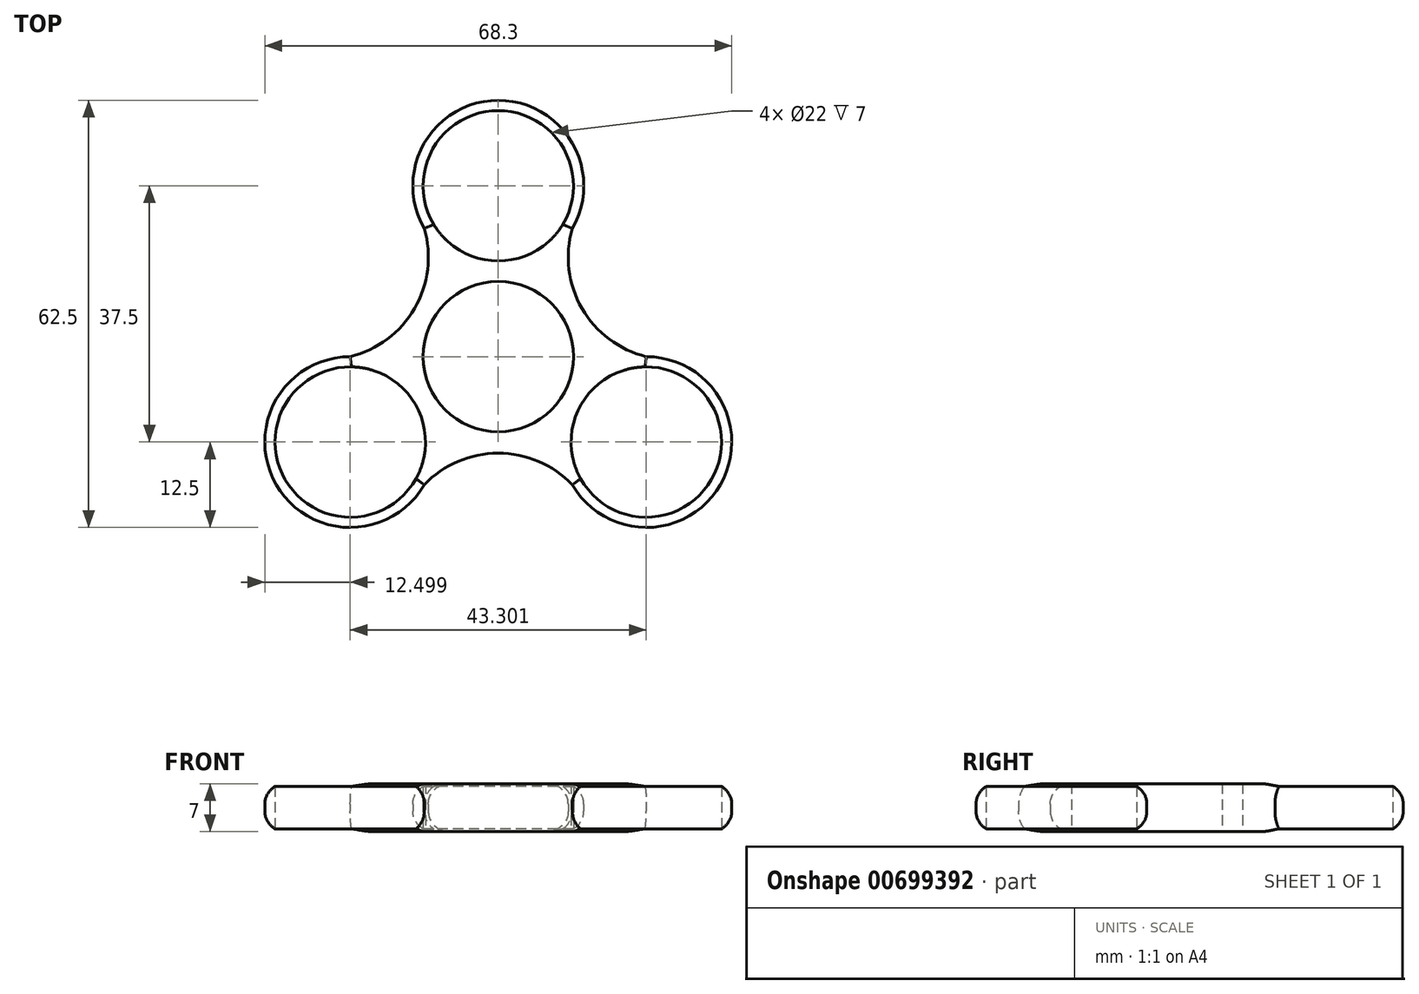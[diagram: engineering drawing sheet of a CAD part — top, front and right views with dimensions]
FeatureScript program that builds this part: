
annotation { "Feature Type Name" : "Feature", "Feature Type Description" : "" }
export const myFeature = defineFeature(function(context is Context, id is Id, definition is map)
    precondition{}
    {
        {
            var Q0;
            Q0=qCreatedBy(makeId("Top.planeOp"),FACE);
            var sketch = newSketch(context, id + "F0", { "sketchPlane" : qUnion([Q0])});
            skCircle(sketch, "E0", {"center": v(0, 0) * mm, "radius": 11 * mm});
            skCircle(sketch, "E1", {"center": v(0, 25) * mm, "radius": 11 * mm});
            skCircle(sketch, "E2", {"center": v(21.65, -12.5) * mm, "radius": 11 * mm});
            skCircle(sketch, "E3", {"center": v(-21.65, -12.5) * mm, "radius": 11 * mm});
            skArc(sketch, "E4", {"start": v(-21.65, 0) * mm, "mid": v(-32.48, -18.75) * mm, "end": v(-10.83, -18.75) * mm});
            skArc(sketch, "E5", {"start": v(10.83, -18.75) * mm, "mid": v(32.48, -18.75) * mm, "end": v(21.65, 0) * mm});
            skArc(sketch, "E6", {"start": v(10.83, 18.75) * mm, "mid": v(0, 37.5) * mm, "end": v(-10.83, 18.75) * mm});
            skArc(sketch, "E7", {"start": v(-21.65, 0) * mm, "mid": v(-12.24, 7.07) * mm, "end": v(-10.83, 18.75) * mm});
            skArc(sketch, "E8", {"start": v(10.83, 18.75) * mm, "mid": v(12.24, 7.07) * mm, "end": v(21.65, 0) * mm});
            skArc(sketch, "E9", {"start": v(10.83, -18.75) * mm, "mid": v(0, -14.13) * mm, "end": v(-10.83, -18.75) * mm});
            skSolve(sketch);
        }
        {
            var Q0;
            Q0=makeQuery(id+"F0.imprint","IMPRINT",FACE,{"disambiguationData":[TD([[makeQuery(id+"F0.imprint","IMPRINT",EDGE,{"derivedFrom":sQuery(id+"F0.wireOp",EDGE,"E0")}),-1.0]])]});
            extrude(context, id + "F1", {"entities" : qUnion([Q0]), "depth" : 7 * mm, "offsetDistance" : 25 * mm});
        }
        {
            var Q0;
            Q0=makeQuery(id+"F1.opExtrude","CAP_EDGE",EDGE,{"disambiguationData":[OSD([sQuery(id+"F0.wireOp",EDGE,"E4")])],"isStart":false});
            var Q1;
            Q1=makeQuery(id+"F1.opExtrude","CAP_EDGE",EDGE,{"disambiguationData":[OSD([sQuery(id+"F0.wireOp",EDGE,"E9")])],"isStart":false});
            var Q2;
            Q2=makeQuery(id+"F1.opExtrude","CAP_EDGE",EDGE,{"disambiguationData":[OSD([sQuery(id+"F0.wireOp",EDGE,"E5")])],"isStart":false});
            var Q3;
            Q3=makeQuery(id+"F1.opExtrude","CAP_EDGE",EDGE,{"disambiguationData":[OSD([sQuery(id+"F0.wireOp",EDGE,"E8")])],"isStart":false});
            var Q4;
            Q4=makeQuery(id+"F1.opExtrude","CAP_EDGE",EDGE,{"disambiguationData":[OSD([sQuery(id+"F0.wireOp",EDGE,"E6")])],"isStart":false});
            var Q5;
            Q5=makeQuery(id+"F1.opExtrude","CAP_EDGE",EDGE,{"disambiguationData":[OSD([sQuery(id+"F0.wireOp",EDGE,"E7")])],"isStart":false});
            var Q6;
            Q6=makeQuery(id+"F1.opExtrude","CAP_EDGE",EDGE,{"disambiguationData":[OSD([sQuery(id+"F0.wireOp",EDGE,"E6")])],"isStart":true});
            var Q7;
            Q7=makeQuery(id+"F1.opExtrude","CAP_EDGE",EDGE,{"disambiguationData":[OSD([sQuery(id+"F0.wireOp",EDGE,"E8")])],"isStart":true});
            var Q8;
            Q8=makeQuery(id+"F1.opExtrude","CAP_EDGE",EDGE,{"disambiguationData":[OSD([sQuery(id+"F0.wireOp",EDGE,"E5")])],"isStart":true});
            var Q9;
            Q9=makeQuery(id+"F1.opExtrude","CAP_EDGE",EDGE,{"disambiguationData":[OSD([sQuery(id+"F0.wireOp",EDGE,"E9")])],"isStart":true});
            var Q10;
            Q10=makeQuery(id+"F1.opExtrude","CAP_EDGE",EDGE,{"disambiguationData":[OSD([sQuery(id+"F0.wireOp",EDGE,"E4")])],"isStart":true});
            var Q11;
            Q11=makeQuery(id+"F1.opExtrude","CAP_EDGE",EDGE,{"disambiguationData":[OSD([sQuery(id+"F0.wireOp",EDGE,"E7")])],"isStart":true});
            fillet(context, id + "F2", {"entities" : qUnion([Q0, Q1, Q2, Q3, Q4, Q5, Q6, Q7, Q8, Q9, Q10, Q11]), "radius" : 3 * mm, "tangentPropagation" : true, "allowEdgeOverflow" : false});
        }
    });
